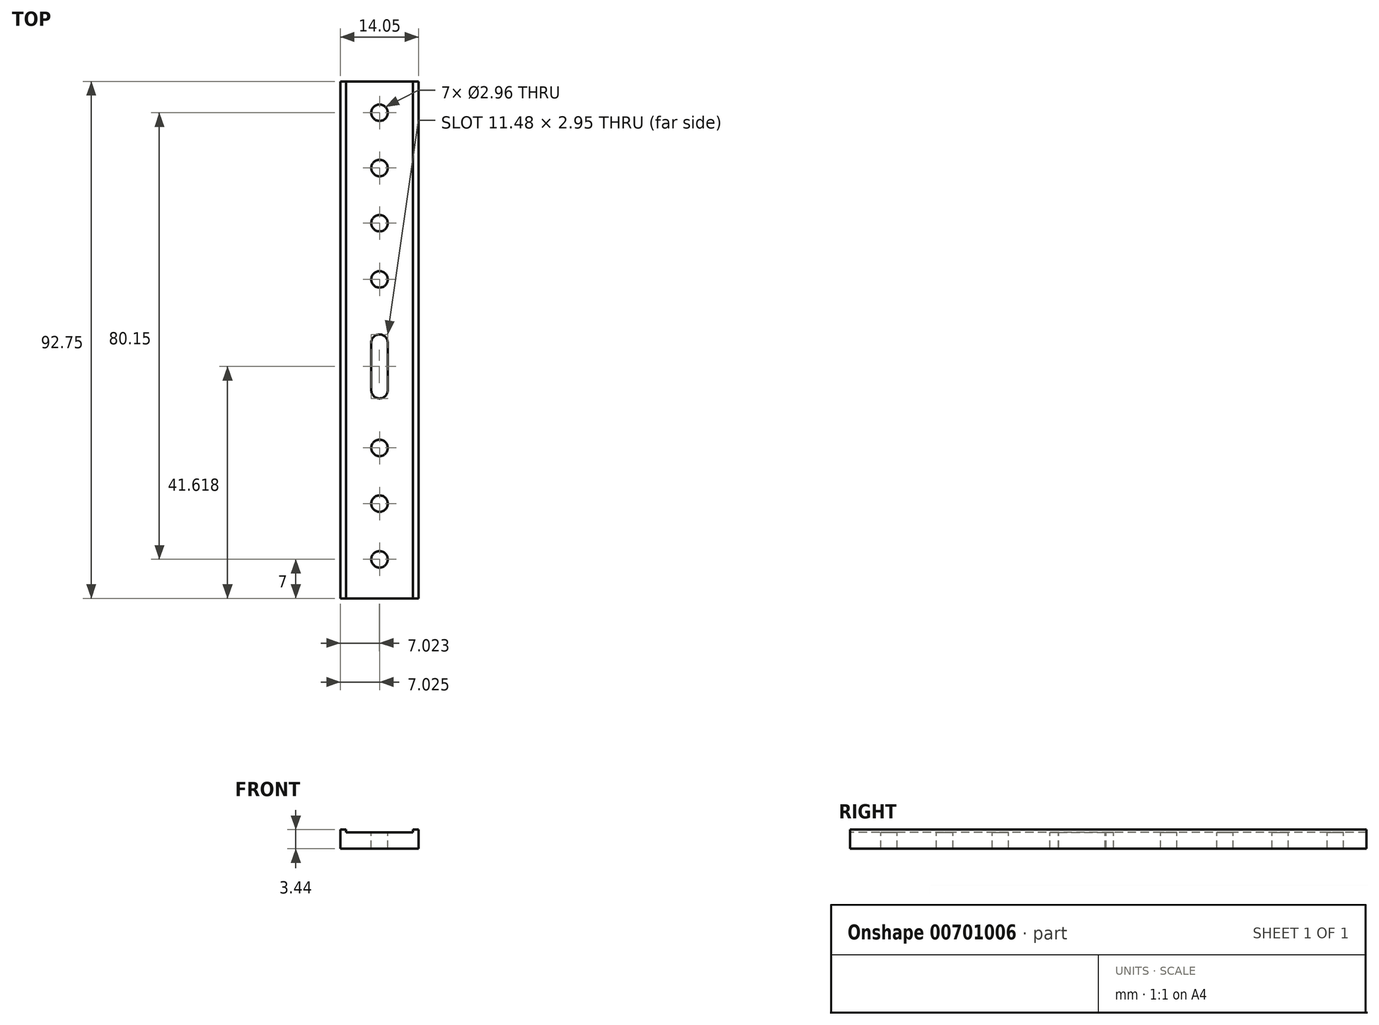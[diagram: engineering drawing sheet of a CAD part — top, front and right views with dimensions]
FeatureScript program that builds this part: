
annotation { "Feature Type Name" : "Feature", "Feature Type Description" : "" }
export const myFeature = defineFeature(function(context is Context, id is Id, definition is map)
    precondition{}
    {
        {
            var Q0;
            Q0=qCreatedBy(makeId("Top.planeOp"),FACE);
            var sketch = newSketch(context, id + "F0", { "sketchPlane" : qUnion([Q0])});
            skLineSegment(sketch, "E0.bottom", {"start": v(0, 0) * mm, "end": v(14.05, 0) * mm});
            skLineSegment(sketch, "E0.top", {"start": v(0, 92.75) * mm, "end": v(14.05, 92.75) * mm});
            skLineSegment(sketch, "E0.left", {"start": v(0, 0) * mm, "end": v(0, 92.75) * mm});
            skLineSegment(sketch, "E0.right", {"start": v(14.05, 0) * mm, "end": v(14.05, 92.75) * mm});
            skSolve(sketch);
        }
        {
            var Q0;
            Q0 = qSketchRegion(id + "F0", true);
            extrude(context, id + "F1", {"entities" : qUnion([Q0]), "depth" : 2.94 * mm, "offsetDistance" : 25 * mm});
        }
        {
            var Q0;
            Q0=makeQuery(id+"F1.opExtrude","CAP_FACE",FACE,{"disambiguationData":[OSD([sQuery(id+"F0.wireOp",EDGE,"E0.bottom"),sQuery(id+"F0.wireOp",EDGE,"E0.top"),sQuery(id+"F0.wireOp",EDGE,"E0.left"),sQuery(id+"F0.wireOp",EDGE,"E0.right")])],"isStart":false});
            var sketch = newSketch(context, id + "F2", { "sketchPlane" : qUnion([Q0])});
            skLineSegment(sketch, "E1.bottom", {"start": v(0, 92.75) * mm, "end": v(1.05, 92.75) * mm});
            skLineSegment(sketch, "E1.top", {"start": v(0, 0) * mm, "end": v(1.05, 0) * mm});
            skLineSegment(sketch, "E1.left", {"start": v(0, 92.75) * mm, "end": v(0, 0) * mm});
            skLineSegment(sketch, "E1.right", {"start": v(1.05, 92.75) * mm, "end": v(1.05, 0) * mm});
            skLineSegment(sketch, "E2.bottom", {"start": v(14.05, 92.75) * mm, "end": v(13, 92.75) * mm});
            skLineSegment(sketch, "E2.top", {"start": v(14.05, 0) * mm, "end": v(13, 0) * mm});
            skLineSegment(sketch, "E2.left", {"start": v(14.05, 92.75) * mm, "end": v(14.05, 0) * mm});
            skLineSegment(sketch, "E2.right", {"start": v(13, 92.75) * mm, "end": v(13, 0) * mm});
            skSolve(sketch);
        }
        {
            var Q0;
            Q0 = qSketchRegion(id + "F2", true);
            extrude(context, id + "F3", {"entities" : qUnion([Q0]), "operationType" : NewBodyOperationType.ADD, "depth" : 0.5 * mm, "offsetDistance" : 25 * mm});
        }
        {
            var Q0;
            Q0=makeQuery(id+"F1.opExtrude","CAP_FACE",FACE,{"disambiguationData":[OSD([sQuery(id+"F0.wireOp",EDGE,"E0.bottom"),sQuery(id+"F0.wireOp",EDGE,"E0.top"),sQuery(id+"F0.wireOp",EDGE,"E0.left"),sQuery(id+"F0.wireOp",EDGE,"E0.right")])],"isStart":false});
            var sketch = newSketch(context, id + "F4", { "sketchPlane" : qUnion([Q0])});
            skArc(sketch, "E3", {"start": v(5.55, 37.44) * mm, "mid": v(7.06, 35.88) * mm, "end": v(8.5, 37.5) * mm});
            skArc(sketch, "E4", {"start": v(8.5, 46.02) * mm, "mid": v(6.92, 47.36) * mm, "end": v(5.55, 45.8) * mm});
            skLineSegment(sketch, "E5", {"start": v(5.55, 37.44) * mm, "end": v(5.55, 45.8) * mm});
            skLineSegment(sketch, "E6", {"start": v(8.5, 37.5) * mm, "end": v(8.5, 46.02) * mm});
            skCircle(sketch, "E7", {"center": v(7.02, 87.15) * mm, "radius": 1.48 * mm});
            skCircle(sketch, "E8", {"center": v(7.02, 77.23) * mm, "radius": 1.48 * mm});
            skCircle(sketch, "E9", {"center": v(7.02, 67.33) * mm, "radius": 1.48 * mm});
            skCircle(sketch, "E10", {"center": v(7.02, 57.24) * mm, "radius": 1.48 * mm});
            skCircle(sketch, "E11", {"center": v(7.03, 7) * mm, "radius": 1.48 * mm});
            skCircle(sketch, "E12", {"center": v(7.03, 17) * mm, "radius": 1.48 * mm});
            skCircle(sketch, "E13", {"center": v(7.03, 27) * mm, "radius": 1.48 * mm});
            skSolve(sketch);
        }
        {
            var Q0;
            Q0 = qSketchRegion(id + "F4", true);
            extrude(context, id + "F5", {"entities" : qUnion([Q0]), "operationType" : NewBodyOperationType.REMOVE, "endBound" : BoundingType.THROUGH_ALL, "oppositeDirection" : true, "depth" : 25 * mm, "offsetDistance" : 25 * mm});
        }
    });
